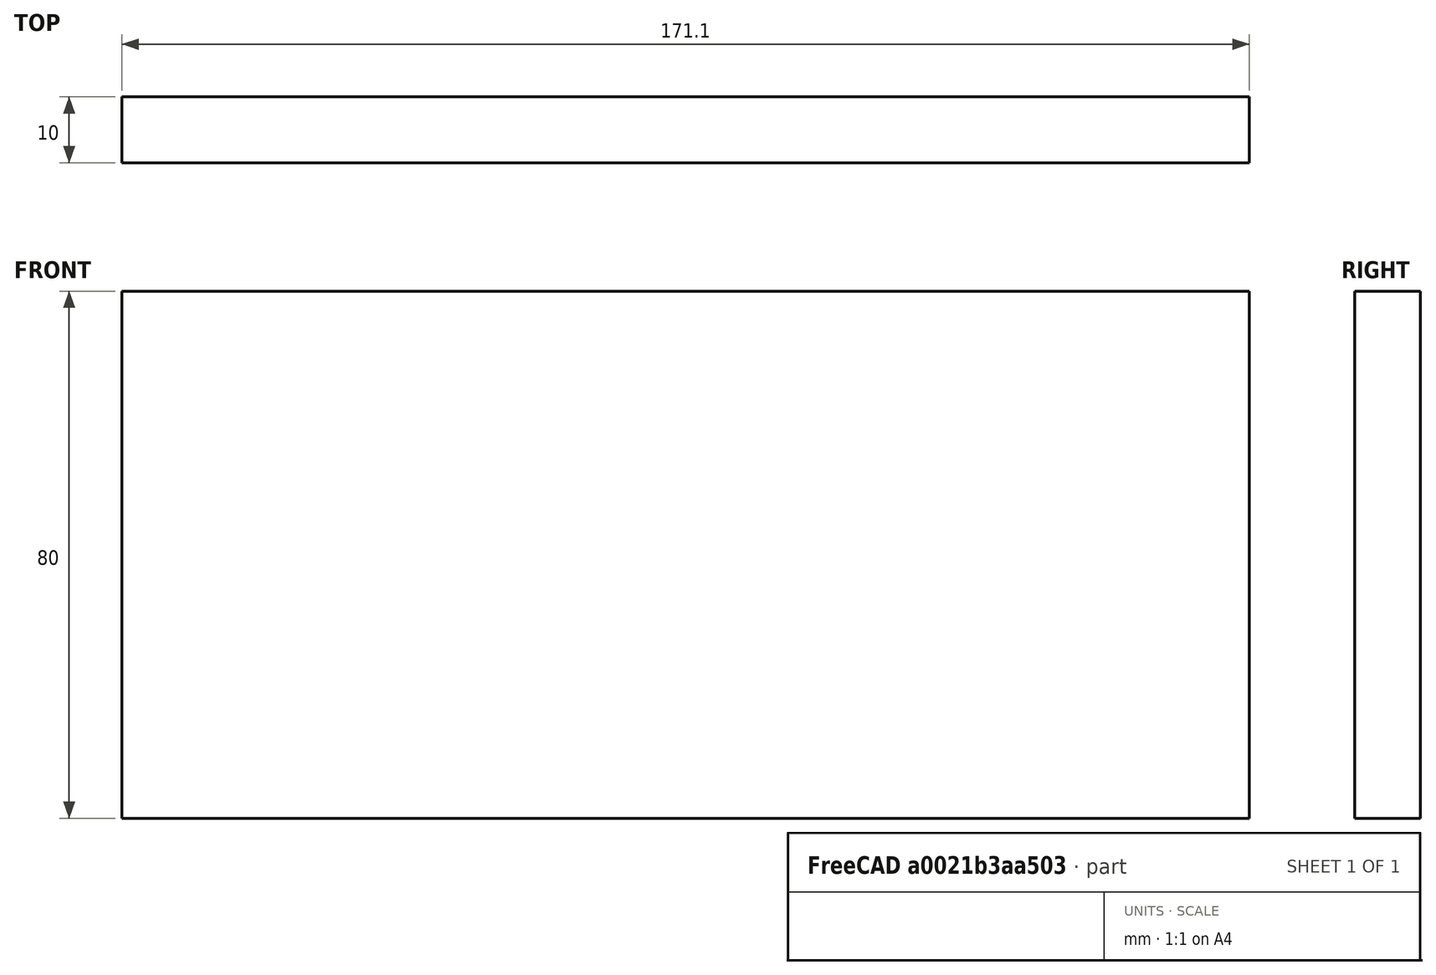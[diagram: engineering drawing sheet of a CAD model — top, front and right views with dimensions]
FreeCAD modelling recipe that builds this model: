
FCSTD DOCUMENT  (FreeCAD 0.21R33771 (Git))
Label: Side_Panel-A
License: All rights reserved
LicenseURL: http://en.wikipedia.org/wiki/All_rights_reserved
objects: Sketcher::SketchObject×1, PartDesign::Pad×1, PartDesign::CoordinateSystem×1, PartDesign::Body×1
note: 5 computed .brp shape members not serialized (recipe doc carries the construction recipe); baked Part::Feature solids carry a one-line shape summary decoded from their .brp
EXTERNAL_REF file=Noise_Toaster_Classic.FCStd obj=Spreadsheet

FEATURE [Sketcher::SketchObject] Sketch
  FullyConstrained = true
  MapMode = 5
  Placement = pos=(0,0,0) rot=(1,0,0;1.5708rad)
  Support = -> [XZ_Plane]
  expr: Constraints[10] = Noise_Toaster_Classic#<<measurements>>.Side_A_height
  expr: Constraints[9] = Noise_Toaster_Classic#<<measurements>>.Side_A_width
  sketch-geometry (4):
    g0: LineSegment StartX=0 StartY=0 StartZ=0 EndX=171.1 EndY=0 EndZ=0
    g1: LineSegment StartX=171.1 StartY=0 StartZ=0 EndX=171.1 EndY=80 EndZ=0
    g2: LineSegment StartX=171.1 StartY=80 StartZ=0 EndX=0 EndY=80 EndZ=0
    g3: LineSegment StartX=0 StartY=80 StartZ=0 EndX=0 EndY=0 EndZ=0
  constraints (11):
    c: Coincident(g0,g1)
    c: Coincident(g1,g2)
    c: Coincident(g2,g3)
    c: Coincident(g3,g0)
    c: Horizontal(g0)
    c: Horizontal(g2)
    c: Vertical(g1)
    c: Vertical(g3)
    c: Coincident(g0,g-1)
    c: DistanceX(g2,g2) = 171.1
    c: DistanceY(g3,g3) = 80
FEATURE [PartDesign::Pad] Pad
  Direction = (0,-1,-2e-16)
  Length = 10
  Length2 = 10
  Placement = pos=(0,0,0) rot=(1,0,0;1.5708rad)
  Profile = -> Sketch
  ReferenceAxis = -> Sketch [N_Axis]
  Type = 0
  expr: Length = Noise_Toaster_Classic#<<measurements>>.Side_A_thickness
FEATURE [PartDesign::CoordinateSystem] SP_A_LCS
  AttacherType = Attacher::AttachEngine3D
  Support = -> [Pad]
FEATURE [PartDesign::Body] Body  label="Körper"
  Group = -> [Sketch,Pad,SP_A_LCS]
  Origin = -> Origin
  Tip = -> Pad
